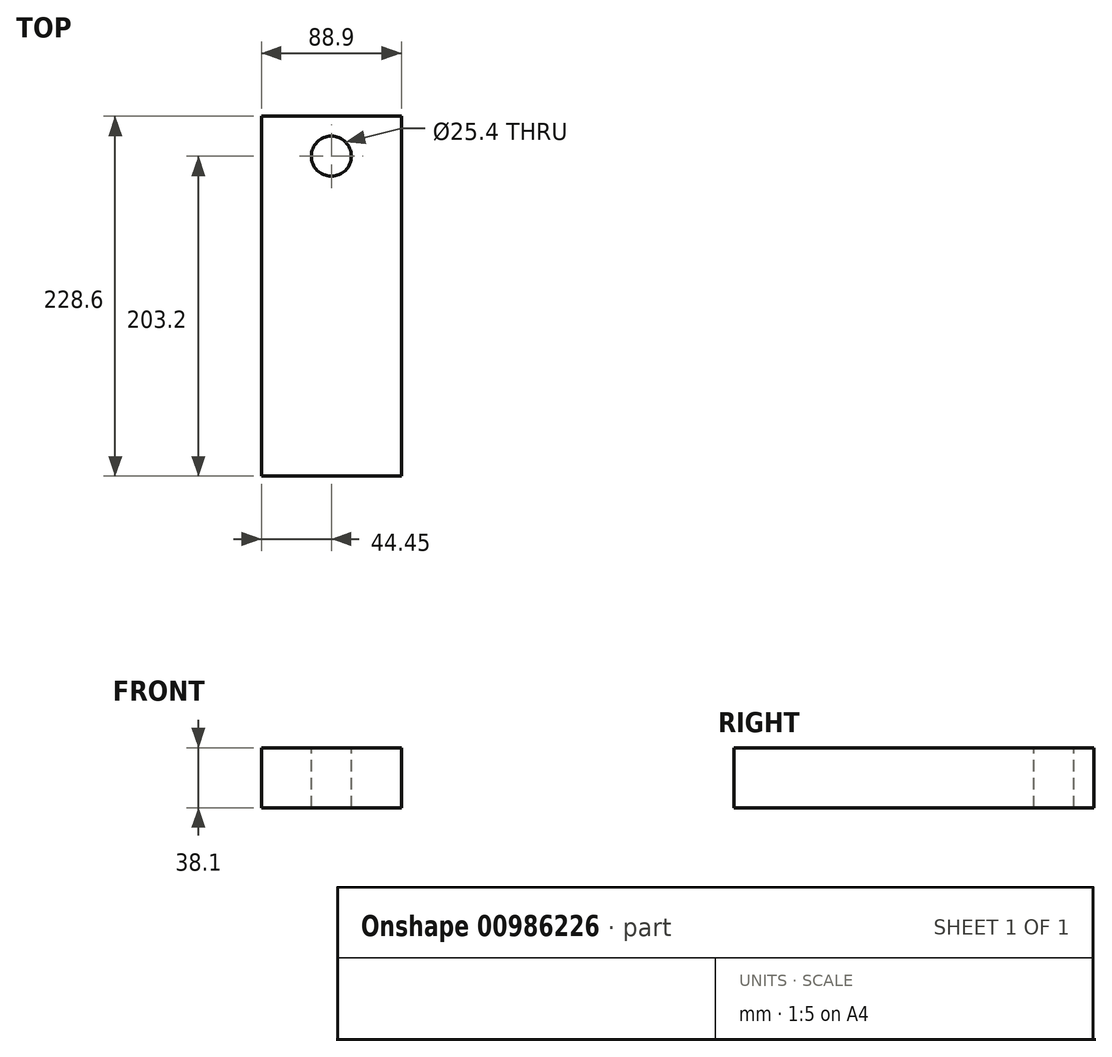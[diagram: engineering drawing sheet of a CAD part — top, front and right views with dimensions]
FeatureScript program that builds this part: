
annotation { "Feature Type Name" : "Feature", "Feature Type Description" : "" }
export const myFeature = defineFeature(function(context is Context, id is Id, definition is map)
    precondition{}
    {
        {
            var Q0;
            Q0=qCreatedBy(makeId("Front.planeOp"),FACE);
            var sketch = newSketch(context, id + "F0", { "sketchPlane" : qUnion([Q0])});
            skLineSegment(sketch, "E0.bottom", {"start": v(0, 0) * mm, "end": v(88.9, 0) * mm});
            skLineSegment(sketch, "E0.top", {"start": v(0, 38.1) * mm, "end": v(88.9, 38.1) * mm});
            skLineSegment(sketch, "E0.left", {"start": v(0, 0) * mm, "end": v(0, 38.1) * mm});
            skLineSegment(sketch, "E0.right", {"start": v(88.9, 0) * mm, "end": v(88.9, 38.1) * mm});
            skSolve(sketch);
        }
        {
            var Q0;
            Q0=makeQuery(id+"F0.imprint","IMPRINT",FACE,{"disambiguationData":[TD([[makeQuery(id+"F0.imprint","IMPRINT",EDGE,{"derivedFrom":sQuery(id+"F0.wireOp",EDGE,"E0.bottom")}),1.0]])]});
            extrude(context, id + "F1", {"entities" : qUnion([Q0]), "depth" : 228.6 * mm, "offsetDistance" : 25.4 * mm});
        }
        {
            var Q0;
            Q0=makeQuery(id+"F1.opExtrude","SWEPT_FACE",FACE,{"disambiguationData":[OSD([sQuery(id+"F0.wireOp",EDGE,"E0.top")])]});
            var sketch = newSketch(context, id + "F2", { "sketchPlane" : qUnion([Q0])});
            skCircle(sketch, "E1", {"center": v(44.45, -25.4) * mm, "radius": 12.7 * mm});
            skPoint(sketch, "E1.centerSnap0", {"position": v(44.45, 0) * mm});
            skSolve(sketch);
        }
        {
            var Q0;
            Q0=makeQuery(id+"F2.imprint","IMPRINT",FACE,{"disambiguationData":[TD([[makeQuery(id+"F2.imprint","IMPRINT",EDGE,{"derivedFrom":sQuery(id+"F2.wireOp",EDGE,"E1")}),1.0]])]});
            extrude(context, id + "F3", {"entities" : qUnion([Q0]), "operationType" : NewBodyOperationType.REMOVE, "endBound" : BoundingType.THROUGH_ALL, "oppositeDirection" : true, "depth" : 25.4 * mm, "offsetDistance" : 25.4 * mm});
        }
    });
